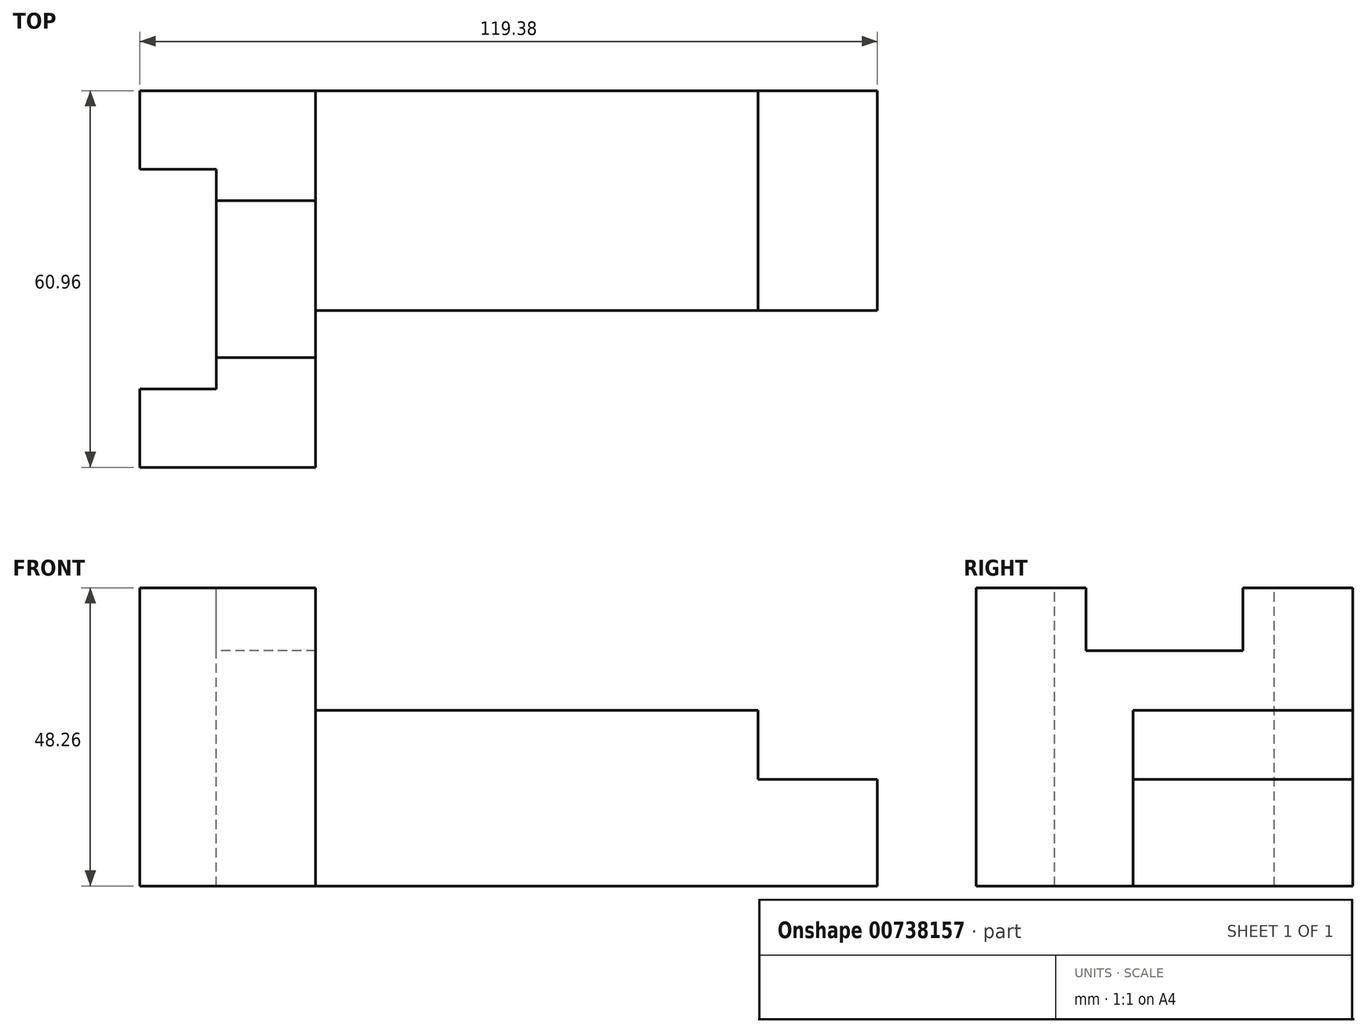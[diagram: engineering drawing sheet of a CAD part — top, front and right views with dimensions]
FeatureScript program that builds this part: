
annotation { "Feature Type Name" : "Feature", "Feature Type Description" : "" }
export const myFeature = defineFeature(function(context is Context, id is Id, definition is map)
    precondition{}
    {
        {
            var Q0;
            Q0=qCreatedBy(makeId("Front.planeOp"),FACE);
            var sketch = newSketch(context, id + "F0", { "sketchPlane" : qUnion([Q0])});
            skLineSegment(sketch, "E0", {"start": v(-71.06, 56.37) * mm, "end": v(-42.61, 56.37) * mm});
            skLineSegment(sketch, "E1", {"start": v(-42.61, 56.37) * mm, "end": v(-42.61, 36.56) * mm});
            skLineSegment(sketch, "E2", {"start": v(-42.61, 36.56) * mm, "end": v(29.02, 36.56) * mm});
            skLineSegment(sketch, "E3", {"start": v(29.02, 36.56) * mm, "end": v(29.02, 25.39) * mm});
            skLineSegment(sketch, "E4", {"start": v(29.02, 25.39) * mm, "end": v(48.32, 25.39) * mm});
            skLineSegment(sketch, "E5", {"start": v(48.32, 25.39) * mm, "end": v(48.32, 8.11) * mm});
            skLineSegment(sketch, "E6", {"start": v(48.32, 8.11) * mm, "end": v(-42.61, 8.11) * mm});
            skLineSegment(sketch, "E7", {"start": v(-42.61, 8.11) * mm, "end": v(-71.06, 8.11) * mm});
            skLineSegment(sketch, "E8", {"start": v(-71.06, 8.11) * mm, "end": v(-71.06, 56.37) * mm});
            skLineSegment(sketch, "E9", {"start": v(-42.61, 36.56) * mm, "end": v(-42.61, 8.11) * mm});
            skSolve(sketch);
        }
        {
            var Q0;
            Q0=makeQuery(id+"F0.imprint","IMPRINT",FACE,{"disambiguationData":[TD([[makeQuery(id+"F0.imprint","IMPRINT",EDGE,{"derivedFrom":sQuery(id+"F0.wireOp",EDGE,"E0")}),-1.0]])]});
            extrude(context, id + "F1", {"entities" : qUnion([Q0]), "depth" : 60.96 * mm, "offsetDistance" : 25.4 * mm});
        }
        {
            var Q0;
            Q0=makeQuery(id+"F1.opExtrude","SWEPT_FACE",FACE,{"disambiguationData":[OSD([sQuery(id+"F0.wireOp",EDGE,"E0")])]});
            var sketch = newSketch(context, id + "F2", { "sketchPlane" : qUnion([Q0])});
            skLineSegment(sketch, "E10", {"start": v(-42.61, -17.78) * mm, "end": v(-58.68, -17.78) * mm});
            skLineSegment(sketch, "E11", {"start": v(-58.68, -17.78) * mm, "end": v(-58.68, -43.18) * mm});
            skLineSegment(sketch, "E12", {"start": v(-58.68, -43.18) * mm, "end": v(-42.61, -43.18) * mm});
            skLineSegment(sketch, "E13", {"start": v(-58.68, -17.78) * mm, "end": v(-58.68, -12.7) * mm});
            skLineSegment(sketch, "E14", {"start": v(-58.68, -12.7) * mm, "end": v(-71.06, -12.7) * mm});
            skLineSegment(sketch, "E15", {"start": v(-58.68, -43.18) * mm, "end": v(-58.68, -48.26) * mm});
            skLineSegment(sketch, "E16", {"start": v(-58.68, -48.26) * mm, "end": v(-71.06, -48.26) * mm});
            skSolve(sketch);
        }
        {
            var Q0;
            Q0=makeQuery(id+"F0.imprint","IMPRINT",FACE,{"disambiguationData":[TD([[makeQuery(id+"F0.imprint","IMPRINT",EDGE,{"derivedFrom":sQuery(id+"F0.wireOp",EDGE,"E2")}),-1.0]])]});
            extrude(context, id + "F3", {"entities" : qUnion([Q0]), "depth" : 35.56 * mm, "offsetDistance" : 25.4 * mm});
        }
        {
            var Q0;
            {var subQ0=sQuery(id+"F2.wireOp",EDGE,"E10");Q0=makeQuery(id+"F2.imprint","IMPRINT",FACE,{"disambiguationData":[TD([[makeQuery(id+"F2.imprint","IMPRINT",EDGE,{"derivedFrom":subQ0}),1.0]])]});}
            extrude(context, id + "F4", {"entities" : qUnion([Q0]), "operationType" : NewBodyOperationType.REMOVE, "oppositeDirection" : true, "depth" : 10.16 * mm, "offsetDistance" : 25.4 * mm});
        }
        {
            var Q0;
            Q0=makeQuery(id+"F2.imprint","IMPRINT",FACE,{"disambiguationData":[TD([[makeQuery(id+"F2.imprint","IMPRINT",EDGE,{"derivedFrom":sQuery(id+"F2.wireOp",EDGE,"E11")}),-1.0]])]});
            extrude(context, id + "F5", {"entities" : qUnion([Q0]), "operationType" : NewBodyOperationType.REMOVE, "oppositeDirection" : true, "depth" : 48.26 * mm, "offsetDistance" : 25.4 * mm});
        }
    });
